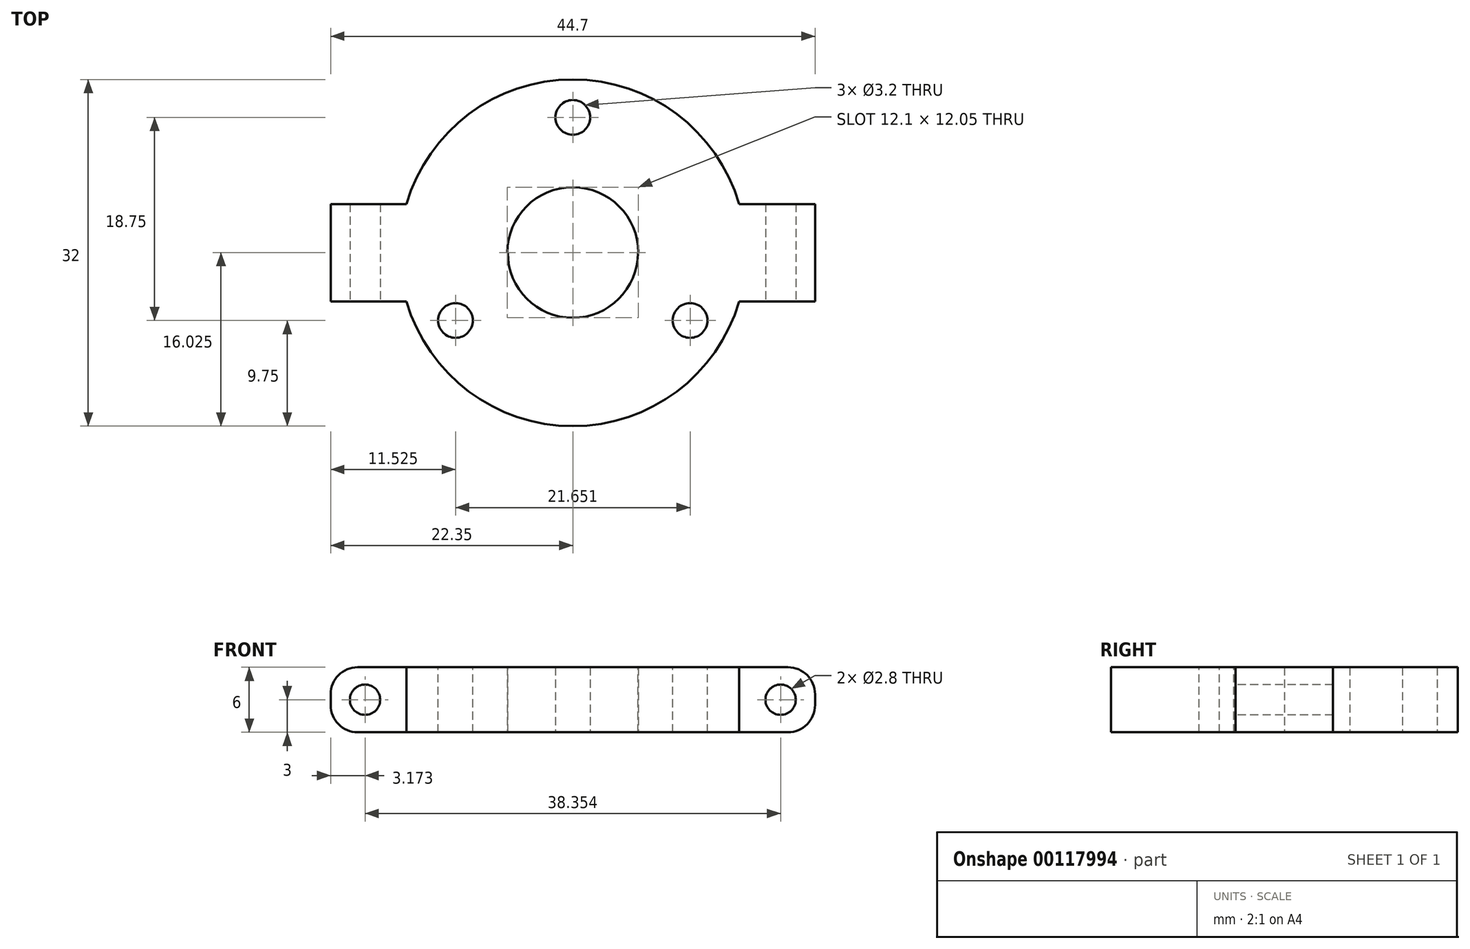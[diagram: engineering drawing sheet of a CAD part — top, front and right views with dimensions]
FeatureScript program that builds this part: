
annotation { "Feature Type Name" : "Feature", "Feature Type Description" : "" }
export const myFeature = defineFeature(function(context is Context, id is Id, definition is map)
    precondition{}
    {
        {
            var Q0;
            Q0=qCreatedBy(makeId("Top.planeOp"),FACE);
            var sketch = newSketch(context, id + "F0", { "sketchPlane" : qUnion([Q0])});
            skArc(sketch, "E0", {"start": v(6.05, -14.81) * mm, "mid": v(0, 16) * mm, "end": v(-6.05, -14.81) * mm});
            skLineSegment(sketch, "E1", {"start": v(0, 12.5) * mm, "end": v(0, 0) * mm, "construction": true});
            skLineSegment(sketch, "E2", {"start": v(0, 0) * mm, "end": v(-10.83, -6.25) * mm, "construction": true});
            skLineSegment(sketch, "E3", {"start": v(0, 0) * mm, "end": v(10.83, -6.25) * mm, "construction": true});
            skCircle(sketch, "E4", {"center": v(0, 12.5) * mm, "radius": 1.6 * mm});
            skCircle(sketch, "E5", {"center": v(10.83, -6.25) * mm, "radius": 1.6 * mm});
            skCircle(sketch, "E6", {"center": v(-10.83, -6.25) * mm, "radius": 1.6 * mm});
            skArc(sketch, "E7", {"start": v(6.05, 0) * mm, "mid": v(0, 6.05) * mm, "end": v(-6.05, 0) * mm});
            skArc(sketch, "E8", {"start": v(7.65, 0) * mm, "mid": v(0, 7.65) * mm, "end": v(-7.65, 0) * mm});
            skLineSegment(sketch, "E9", {"start": v(-6.05, 0) * mm, "end": v(-6.05, -14.81) * mm});
            skLineSegment(sketch, "E10", {"start": v(6.05, 0) * mm, "end": v(6.05, -14.81) * mm});
            skLineSegment(sketch, "E11", {"start": v(-16, 0) * mm, "end": v(16, 0) * mm});
            skLineSegment(sketch, "E12", {"start": v(-7.65, 0) * mm, "end": v(-6.05, 0) * mm});
            skLineSegment(sketch, "E13", {"start": v(6.05, 0) * mm, "end": v(7.65, 0) * mm});
            skLineSegment(sketch, "E14", {"start": v(16, 0) * mm, "end": v(22.35, 0) * mm});
            skLineSegment(sketch, "E15", {"start": v(22.35, 0) * mm, "end": v(22.35, 4.5) * mm});
            skLineSegment(sketch, "E16", {"start": v(22.35, 4.5) * mm, "end": v(15.35, 4.5) * mm});
            skLineSegment(sketch, "E17", {"start": v(-16, 0) * mm, "end": v(-22.35, 0) * mm});
            skLineSegment(sketch, "E18", {"start": v(-22.35, 0) * mm, "end": v(-22.35, 4.5) * mm});
            skLineSegment(sketch, "E19", {"start": v(-22.35, 4.5) * mm, "end": v(-15.35, 4.5) * mm});
            skCircle(sketch, "E20", {"center": v(-10.83, -6.25) * mm, "radius": 2.95 * mm, "construction": true});
            skSolve(sketch);
        }
        {
            var Q0;
            {var subQ0=sQuery(id+"F0.wireOp",EDGE,"E17");Q0=makeQuery(id+"F0.imprint","IMPRINT",FACE,{"disambiguationData":[TD([[makeQuery(id+"F0.imprint","IMPRINT",EDGE,{"derivedFrom":subQ0}),-1.0]])]});}
            var Q1;
            Q1=makeQuery(id+"F0.imprint","IMPRINT",FACE,{"disambiguationData":[TD([[makeQuery(id+"F0.imprint","IMPRINT",EDGE,{"derivedFrom":sQuery(id+"F0.wireOp",EDGE,"E4")}),-1.0]])]});
            var Q2;
            Q2=makeQuery(id+"F0.imprint","IMPRINT",FACE,{"disambiguationData":[TD([[makeQuery(id+"F0.imprint","IMPRINT",EDGE,{"derivedFrom":sQuery(id+"F0.wireOp",EDGE,"E7")}),-1.0]])]});
            var Q3;
            {var subQ0=sQuery(id+"F0.wireOp",EDGE,"E14");Q3=makeQuery(id+"F0.imprint","IMPRINT",FACE,{"disambiguationData":[TD([[makeQuery(id+"F0.imprint","IMPRINT",EDGE,{"derivedFrom":subQ0}),1.0]])]});}
            extrude(context, id + "F1", {"entities" : qUnion([Q0, Q1, Q2, Q3]), "depth" : 3 * mm});
        }
        {
            var Q0;
            Q0=makeQuery(id+"F0.imprint","IMPRINT",FACE,{"disambiguationData":[TD([[makeQuery(id+"F0.imprint","IMPRINT",EDGE,{"derivedFrom":sQuery(id+"F0.wireOp",EDGE,"E4")}),-1.0]])]});
            var Q1;
            Q1=makeQuery(id+"F0.imprint","IMPRINT",FACE,{"disambiguationData":[TD([[makeQuery(id+"F0.imprint","IMPRINT",EDGE,{"derivedFrom":sQuery(id+"F0.wireOp",EDGE,"E7")}),-1.0]])]});
            var Q2;
            {var subQ0=sQuery(id+"F0.wireOp",EDGE,"E14");Q2=makeQuery(id+"F0.imprint","IMPRINT",FACE,{"disambiguationData":[TD([[makeQuery(id+"F0.imprint","IMPRINT",EDGE,{"derivedFrom":subQ0}),1.0]])]});}
            var Q3;
            {var subQ0=sQuery(id+"F0.wireOp",EDGE,"E17");Q3=makeQuery(id+"F0.imprint","IMPRINT",FACE,{"disambiguationData":[TD([[makeQuery(id+"F0.imprint","IMPRINT",EDGE,{"derivedFrom":subQ0}),-1.0]])]});}
            extrude(context, id + "F2", {"entities" : qUnion([Q0, Q1, Q2, Q3]), "operationType" : NewBodyOperationType.ADD, "oppositeDirection" : true, "depth" : 3 * mm});
        }
        {
            var Q0;
            {var subQ0=sQuery(id+"F0.wireOp",EDGE,"E17");Q0=makeQuery(id+"F2.boolean.opBoolean","MERGE",FACE,{"derivedFrom":[makeQuery(id+"F1.opExtrude","SWEPT_FACE",FACE,{"disambiguationData":[OSD([subQ0])]}),makeQuery(id+"F2.opExtrude","SWEPT_FACE",FACE,{"disambiguationData":[OSD([sQuery(id+"F0.wireOp",EDGE,"E11"),sQuery(id+"F0.wireOp",EDGE,"E12"),subQ0])]})]});}
            var sketch = newSketch(context, id + "F3", { "sketchPlane" : qUnion([Q0])});
            skLineSegment(sketch, "E21", {"start": v(-16, 0) * mm, "end": v(-22.35, 0) * mm, "construction": true});
            skCircle(sketch, "E22", {"center": v(-19.18, 0) * mm, "radius": 1.4 * mm});
            skCircle(sketch, "E23", {"center": v(19.18, 0) * mm, "radius": 1.4 * mm});
            skLineSegment(sketch, "E24", {"start": v(0, 5.67) * mm, "end": v(0, -7.62) * mm, "construction": true});
            skCircle(sketch, "E25", {"center": v(-19.18, 0) * mm, "radius": 2.9 * mm, "construction": true});
            skSolve(sketch);
        }
        {
            var Q0;
            Q0=makeQuery(id+"F3.imprint","IMPRINT",FACE,{"disambiguationData":[TD([[makeQuery(id+"F3.imprint","IMPRINT",EDGE,{"derivedFrom":sQuery(id+"F3.wireOp",EDGE,"E23")}),1.0]])]});
            var Q1;
            Q1=makeQuery(id+"F3.imprint","IMPRINT",FACE,{"disambiguationData":[TD([[makeQuery(id+"F3.imprint","IMPRINT",EDGE,{"derivedFrom":sQuery(id+"F3.wireOp",EDGE,"E22")}),1.0]])]});
            extrude(context, id + "F4", {"entities" : qUnion([Q0, Q1]), "operationType" : NewBodyOperationType.REMOVE, "endBound" : BoundingType.THROUGH_ALL, "oppositeDirection" : true, "depth" : 25 * mm});
        }
        {
            var Q0;
            Q0=makeQuery(id+"F1.opExtrude","CAP_EDGE",EDGE,{"disambiguationData":[OSD([sQuery(id+"F0.wireOp",EDGE,"E18")])],"isStart":true});
            var Q1;
            Q1=makeQuery(id+"F1.opExtrude","CAP_EDGE",EDGE,{"disambiguationData":[OSD([sQuery(id+"F0.wireOp",EDGE,"E18")])],"isStart":false});
            var Q2;
            Q2=makeQuery(id+"F1.opExtrude","CAP_EDGE",EDGE,{"disambiguationData":[OSD([sQuery(id+"F0.wireOp",EDGE,"E15")])],"isStart":true});
            var Q3;
            Q3=makeQuery(id+"F1.opExtrude","CAP_EDGE",EDGE,{"disambiguationData":[OSD([sQuery(id+"F0.wireOp",EDGE,"E15")])],"isStart":false});
            var Q4;
            Q4=makeQuery(id+"F2.opExtrude","CAP_EDGE",EDGE,{"disambiguationData":[OSD([sQuery(id+"F0.wireOp",EDGE,"E18")])],"isStart":false});
            var Q5;
            Q5=makeQuery(id+"F2.opExtrude","CAP_EDGE",EDGE,{"disambiguationData":[OSD([sQuery(id+"F0.wireOp",EDGE,"E15")])],"isStart":false});
            fillet(context, id + "F5", {"entities" : qUnion([Q0, Q1, Q2, Q3, Q4, Q5]), "radius" : 2.5 * mm, "tangentPropagation" : true, "allowEdgeOverflow" : false});
        }
        {
            var Q0;
            Q0=qCreatedBy(makeId("Top.planeOp"),FACE);
            var sketch = newSketch(context, id + "F6", { "sketchPlane" : qUnion([Q0])});
            skArc(sketch, "E26", {"start": v(-6, 0) * mm, "mid": v(0, -6) * mm, "end": v(6, 0) * mm});
            skArc(sketch, "E27", {"start": v(-9, 0) * mm, "mid": v(0, -9) * mm, "end": v(9, 0) * mm});
            skLineSegment(sketch, "E28.0", {"start": v(-16, 0) * mm, "end": v(-22.35, 0) * mm});
            skLineSegment(sketch, "E28.1", {"start": v(-16, 0) * mm, "end": v(-6, 0) * mm});
            skLineSegment(sketch, "E28.2", {"start": v(16, 0) * mm, "end": v(22.35, 0) * mm});
            skLineSegment(sketch, "E29", {"start": v(-22.35, 0) * mm, "end": v(-22.35, -4.5) * mm});
            skLineSegment(sketch, "E30", {"start": v(-22.35, -4.5) * mm, "end": v(-15.35, -4.5) * mm});
            skLineSegment(sketch, "E31", {"start": v(22.35, 0) * mm, "end": v(22.35, -4.5) * mm});
            skLineSegment(sketch, "E32", {"start": v(22.35, -4.5) * mm, "end": v(15.35, -4.5) * mm});
            skLineSegment(sketch, "E33.0", {"start": v(-22.35, 0) * mm, "end": v(-22.35, 4.5) * mm, "construction": true});
            skLineSegment(sketch, "E34.trimOffspring", {"start": v(6, 0) * mm, "end": v(16, 0) * mm});
            skLineSegment(sketch, "E35", {"start": v(0, 0) * mm, "end": v(0, -11.2) * mm, "construction": true});
            skArc(sketch, "E36", {"start": v(-16, 0) * mm, "mid": v(0, -16) * mm, "end": v(16, 0) * mm});
            skCircle(sketch, "E37.0", {"center": v(-10.83, -6.25) * mm, "radius": 1.6 * mm});
            skCircle(sketch, "E38.0", {"center": v(10.83, -6.25) * mm, "radius": 1.6 * mm});
            skSolve(sketch);
        }
        {
            var Q0;
            Q0 = qSketchRegion(id + "F6", true);
            extrude(context, id + "F7", {"entities" : qUnion([Q0]), "oppositeDirection" : true, "depth" : 3 * mm});
        }
        {
            var Q0;
            Q0=makeQuery(id+"F6.imprint","IMPRINT",FACE,{"disambiguationData":[TD([[makeQuery(id+"F6.imprint","IMPRINT",EDGE,{"derivedFrom":sQuery(id+"F6.wireOp",EDGE,"E28.0")}),1.0]])]});
            var Q1;
            Q1=makeQuery(id+"F6.imprint","IMPRINT",FACE,{"disambiguationData":[TD([[makeQuery(id+"F6.imprint","IMPRINT",EDGE,{"derivedFrom":sQuery(id+"F6.wireOp",EDGE,"E28.2")}),-1.0]])]});
            var Q2;
            {var subQ0=sQuery(id+"F6.wireOp",EDGE,"03ZbOcJL-pHxo-W6wo-bXk0-lmQKoTnWW0hg");Q2=makeQuery(id+"F6.imprint","IMPRINT",FACE,{"disambiguationData":[TD([[makeQuery(id+"F6.imprint","IMPRINT",EDGE,{"derivedFrom":subQ0}),-1.0]])]});}
            var Q3;
            {var subQ5=sQuery(id+"F6.wireOp",EDGE,"E27");Q3=makeQuery(id+"F6.imprint","IMPRINT",FACE,{"disambiguationData":[TD([[makeQuery(id+"F6.imprint","IMPRINT",EDGE,{"derivedFrom":subQ5}),-1.0]])]});}
            var Q4;
            {var subQ0=sQuery(id+"F6.wireOp",EDGE,"E26");Q4=makeQuery(id+"F6.imprint","IMPRINT",FACE,{"disambiguationData":[TD([[makeQuery(id+"F6.imprint","IMPRINT",EDGE,{"derivedFrom":subQ0}),-1.0]])]});}
            extrude(context, id + "F8", {"entities" : qUnion([Q0, Q1, Q2, Q3, Q4]), "operationType" : NewBodyOperationType.ADD, "depth" : 3 * mm});
        }
        {
            var Q0;
            {var subQ0=sQuery(id+"F6.wireOp",EDGE,"E30");Q0=makeQuery(id+"F8.boolean.opBoolean","MERGE",FACE,{"derivedFrom":[makeQuery(id+"F7.opExtrude","SWEPT_FACE",FACE,{"disambiguationData":[OSD([subQ0])]}),makeQuery(id+"F8.opExtrude","SWEPT_FACE",FACE,{"disambiguationData":[OSD([subQ0])]})]});}
            var sketch = newSketch(context, id + "F9", { "sketchPlane" : qUnion([Q0])});
            skLineSegment(sketch, "E39", {"start": v(-22.35, 0) * mm, "end": v(-22.35, 0) * mm});
            skLineSegment(sketch, "E40", {"start": v(0, -3.32) * mm, "end": v(0, 4.53) * mm, "construction": true});
            skCircle(sketch, "E41", {"center": v(-19.18, 0) * mm, "radius": 1.4 * mm});
            skCircle(sketch, "E42", {"center": v(19.18, 0) * mm, "radius": 1.4 * mm});
            skSolve(sketch);
        }
        {
            var Q0;
            Q0=makeQuery(id+"F9.imprint","IMPRINT",FACE,{"disambiguationData":[TD([[makeQuery(id+"F9.imprint","IMPRINT",EDGE,{"derivedFrom":sQuery(id+"F9.wireOp",EDGE,"E41")}),1.0]])]});
            var Q1;
            Q1=makeQuery(id+"F9.imprint","IMPRINT",FACE,{"disambiguationData":[TD([[makeQuery(id+"F9.imprint","IMPRINT",EDGE,{"derivedFrom":sQuery(id+"F9.wireOp",EDGE,"E42")}),1.0]])]});
            extrude(context, id + "F10", {"entities" : qUnion([Q0, Q1]), "operationType" : NewBodyOperationType.REMOVE, "oppositeDirection" : true, "depth" : 25 * mm});
        }
        {
            var Q0;
            Q0=makeQuery(id+"F7.opExtrude","SWEPT_EDGE",EDGE,{"disambiguationData":[OSD([sQuery(id+"F6.wireOp",EDGE,"HuQksDJq-gdBk-niVW-qvW6-XMWPdExphO0D"),sQuery(id+"F6.wireOp",EDGE,"ORNrHTX1-PvRE-IZWq-eBVd-NV0TXQDNiJX1"),sQuery(id+"F6.wireOp",EDGE,"3wHpUQzK-NyJk-wPNq-xGfM-1sAWKzzIhuYe")])]});
            var Q1;
            Q1=makeQuery(id+"F7.opExtrude","SWEPT_EDGE",EDGE,{"disambiguationData":[OSD([sQuery(id+"F6.wireOp",EDGE,"fj7lRQxS-rkeU-Y9RG-NZIn-CC8uWcClix1B"),sQuery(id+"F6.wireOp",EDGE,"QufYy0zX-95ib-bDmF-y8VX-g2SRMRM2Gxlg"),sQuery(id+"F6.wireOp",EDGE,"SwjG7QoT-G2Zk-hjTB-oRpV-HsX4pwROvdaW")])]});
            var Q2;
            Q2=makeQuery(id+"F7.opExtrude","SWEPT_EDGE",EDGE,{"disambiguationData":[OSD([sQuery(id+"F6.wireOp",EDGE,"E27"),sQuery(id+"F6.wireOp",EDGE,"ORNrHTX1-PvRE-IZWq-eBVd-NV0TXQDNiJX1")])]});
            var Q3;
            Q3=makeQuery(id+"F7.opExtrude","SWEPT_EDGE",EDGE,{"disambiguationData":[OSD([sQuery(id+"F6.wireOp",EDGE,"E27"),sQuery(id+"F6.wireOp",EDGE,"QufYy0zX-95ib-bDmF-y8VX-g2SRMRM2Gxlg")])]});
            var Q4;
            Q4=makeQuery(id+"F7.opExtrude","CAP_EDGE",EDGE,{"disambiguationData":[OSD([sQuery(id+"F6.wireOp",EDGE,"E31")])],"isStart":false});
            var Q5;
            Q5=makeQuery(id+"F8.opExtrude","CAP_EDGE",EDGE,{"disambiguationData":[OSD([sQuery(id+"F6.wireOp",EDGE,"E31")])],"isStart":false});
            var Q6;
            Q6=makeQuery(id+"F8.opExtrude","CAP_EDGE",EDGE,{"disambiguationData":[OSD([sQuery(id+"F6.wireOp",EDGE,"E29")])],"isStart":false});
            var Q7;
            Q7=makeQuery(id+"F7.opExtrude","CAP_EDGE",EDGE,{"disambiguationData":[OSD([sQuery(id+"F6.wireOp",EDGE,"E29")])],"isStart":false});
            fillet(context, id + "F11", {"entities" : qUnion([Q0, Q1, Q2, Q3, Q4, Q5, Q6, Q7]), "radius" : 2.5 * mm, "tangentPropagation" : true, "allowEdgeOverflow" : false});
        }
    });
